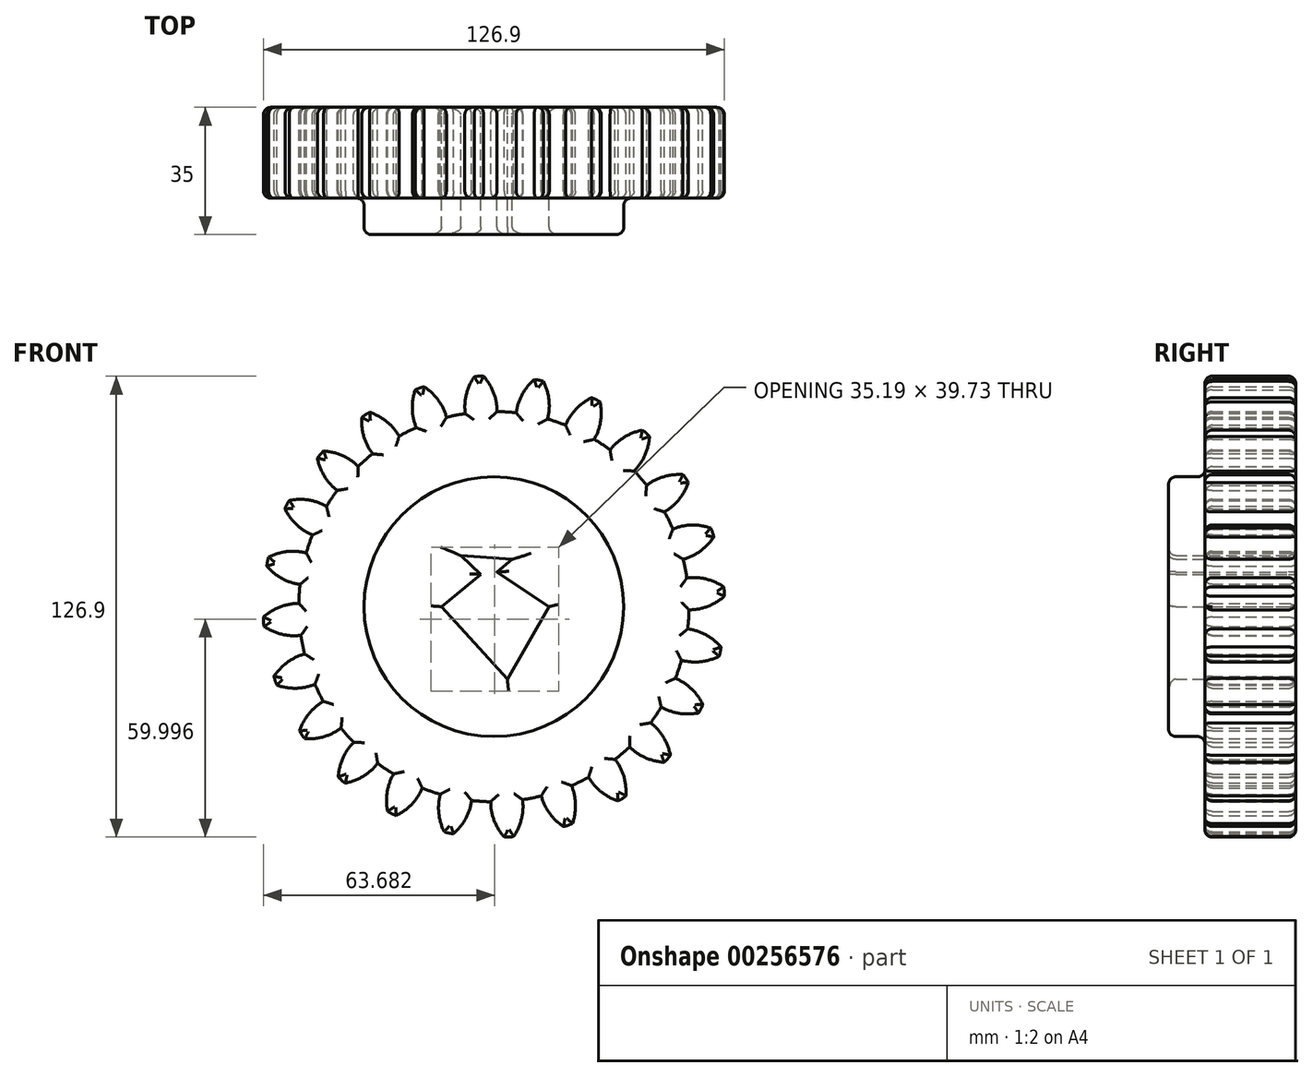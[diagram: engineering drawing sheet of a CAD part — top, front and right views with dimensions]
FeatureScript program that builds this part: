
annotation { "Feature Type Name" : "Feature", "Feature Type Description" : "" }
export const myFeature = defineFeature(function(context is Context, id is Id, definition is map)
    precondition{}
    {
        {
            var Q0;
            Q0=qCreatedBy(makeId("Front.planeOp"),FACE);
            var sketch = newSketch(context, id + "F0", { "sketchPlane" : qUnion([Q0])});
            skCircle(sketch, "E0", {"center": v(0, 0) * mm, "radius": 53.72 * mm});
            skCircle(sketch, "E1", {"center": v(0, 0) * mm, "radius": 58.67 * mm, "construction": true});
            skCircle(sketch, "E2", {"center": v(0, 0) * mm, "radius": 63.5 * mm, "construction": true});
            skLineSegment(sketch, "E3", {"start": v(0, 0) * mm, "end": v(0, 84.4) * mm, "construction": true});
            skLineSegment(sketch, "E4", {"start": v(0, 0) * mm, "end": v(-6.04, 92.1) * mm, "construction": true});
            skLineSegment(sketch, "E5", {"start": v(0, 58.67) * mm, "end": v(-60.72, 58.67) * mm, "construction": true});
            skLineSegment(sketch, "E6", {"start": v(0, 58.67) * mm, "end": v(-60.98, 36.48) * mm, "construction": true});
            skCircle(sketch, "E7", {"center": v(0, 0) * mm, "radius": 55.14 * mm, "construction": true});
            skCircle(sketch, "E8", {"center": v(0, 58.67) * mm, "radius": 14.6 * mm, "construction": true});
            skCircle(sketch, "E9", {"center": v(-13.72, 53.68) * mm, "radius": 14.6 * mm, "construction": true});
            skArc(sketch, "E10", {"start": v(0, 58.67) * mm, "mid": v(-1.2, 61.19) * mm, "end": v(-2.86, 63.44) * mm});
            skArc(sketch, "E11", {"start": v(0.88, 53.71) * mm, "mid": v(0.66, 56.23) * mm, "end": v(0, 58.67) * mm});
            skArc(sketch, "E12.MirrorCS", {"start": v(-7.66, 58.17) * mm, "mid": v(-6.8, 60.82) * mm, "end": v(-5.45, 63.27) * mm});
            skArc(sketch, "E13.MirrorCS", {"start": v(-7.88, 53.14) * mm, "mid": v(-8, 55.67) * mm, "end": v(-7.66, 58.17) * mm});
            skArc(sketch, "E14", {"start": v(-2.86, 63.44) * mm, "mid": v(-4.16, 63.43) * mm, "end": v(-5.45, 63.27) * mm});
            skCircle(sketch, "E15", {"center": v(0, 0) * mm, "radius": 35.75 * mm});
            skLineSegment(sketch, "E16", {"start": v(-3.55, 8.9) * mm, "end": v(-14.46, 0) * mm});
            skLineSegment(sketch, "E17", {"start": v(-14.46, 0) * mm, "end": v(3.69, -19.95) * mm});
            skLineSegment(sketch, "E18", {"start": v(3.69, -19.95) * mm, "end": v(15.16, 0) * mm});
            skLineSegment(sketch, "E19", {"start": v(15.16, 0) * mm, "end": v(0.8, 9.56) * mm});
            skLineSegment(sketch, "E20", {"start": v(0.8, 9.56) * mm, "end": v(5.02, 13.01) * mm});
            skLineSegment(sketch, "E21", {"start": v(-3.55, 8.9) * mm, "end": v(-9.12, 14.01) * mm});
            skLineSegment(sketch, "E22", {"start": v(-9.12, 14.01) * mm, "end": v(5.02, 13.01) * mm});
            skSolve(sketch);
        }
        {
            var Q0;
            {var subQ0=sQuery(id+"F0.wireOp",EDGE,"E0");var subQ1=makeQuery(id+"F0.imprint","INTERSECT",VERTEX,{"derivedFrom":[subQ0,sQuery(id+"F0.wireOp",EDGE,"E11")]});Q0=makeQuery(id+"F0.imprint","IMPRINT",FACE,{"disambiguationData":[TD([[makeQuery(id+"F0.imprint","IMPRINT",EDGE,{"disambiguationData":[TD([[subQ1,-1.0]])],"derivedFrom":subQ0}),1.0]])]});}
            var Q1;
            Q1=makeQuery(id+"F0.imprint","IMPRINT",FACE,{"disambiguationData":[TD([[makeQuery(id+"F0.imprint","IMPRINT",EDGE,{"derivedFrom":sQuery(id+"F0.wireOp",EDGE,"E10")}),1.0]])]});
            extrude(context, id + "F1", {"entities" : qUnion([Q0, Q1]), "depth" : 25 * mm, "offsetDistance" : 25 * mm});
        }
        {
            var Q0;
            Q0=makeQuery(id+"F1.opExtrude","SWEPT_BODY",BODY,{"disambiguationData":[OSD([sQuery(id+"F0.wireOp",EDGE,"E0"),sQuery(id+"F0.wireOp",EDGE,"E10"),sQuery(id+"F0.wireOp",EDGE,"E11"),sQuery(id+"F0.wireOp",EDGE,"E12.MirrorCS"),sQuery(id+"F0.wireOp",EDGE,"E13.MirrorCS"),sQuery(id+"F0.wireOp",EDGE,"E14")])]});
            var Q1;
            Q1=makeQuery(id+"F1.opExtrude","SWEPT_FACE",FACE,{"disambiguationData":[OSD([sQuery(id+"F0.wireOp",EDGE,"E0")])]});
            circularPattern(context, id + "F2", {"entities" : qUnion([Q0]), "axis" : qUnion([Q1]), "angle" : 360 * degree, "instanceCount" : 24, "equalSpace" : true});
        }
        {
            var Q0;
            Q0=makeQuery(id+"F0.imprint","IMPRINT",FACE,{"disambiguationData":[TD([[makeQuery(id+"F0.imprint","IMPRINT",EDGE,{"derivedFrom":sQuery(id+"F0.wireOp",EDGE,"E15")}),1.0]])]});
            extrude(context, id + "F3", {"entities" : qUnion([Q0]), "operationType" : NewBodyOperationType.ADD, "depth" : 35 * mm, "offsetDistance" : 25 * mm});
        }
        {
            var Q0;
            {var subQ0=makeQuery(id+"F1.opExtrude","CAP_FACE",FACE,{"disambiguationData":[OSD([sQuery(id+"F0.wireOp",EDGE,"E0"),sQuery(id+"F0.wireOp",EDGE,"E10"),sQuery(id+"F0.wireOp",EDGE,"E11"),sQuery(id+"F0.wireOp",EDGE,"E12.MirrorCS"),sQuery(id+"F0.wireOp",EDGE,"E13.MirrorCS"),sQuery(id+"F0.wireOp",EDGE,"E14"),sQuery(id+"F0.wireOp",EDGE,"E15")])],"isStart":false});Q0=makeQuery(id+"F3.boolean.opBoolean","MERGE",FACE,{"derivedFrom":[subQ0,makeQuery(id+"F2.opPattern","COPY",FACE,{"derivedFrom":subQ0,"instanceName":"1"}),makeQuery(id+"F2.opPattern","COPY",FACE,{"derivedFrom":subQ0,"instanceName":"2"}),makeQuery(id+"F2.opPattern","COPY",FACE,{"derivedFrom":subQ0,"instanceName":"3"}),makeQuery(id+"F2.opPattern","COPY",FACE,{"derivedFrom":subQ0,"instanceName":"4"}),makeQuery(id+"F2.opPattern","COPY",FACE,{"derivedFrom":subQ0,"instanceName":"5"}),makeQuery(id+"F2.opPattern","COPY",FACE,{"derivedFrom":subQ0,"instanceName":"6"}),makeQuery(id+"F2.opPattern","COPY",FACE,{"derivedFrom":subQ0,"instanceName":"7"}),makeQuery(id+"F2.opPattern","COPY",FACE,{"derivedFrom":subQ0,"instanceName":"8"}),makeQuery(id+"F2.opPattern","COPY",FACE,{"derivedFrom":subQ0,"instanceName":"9"}),makeQuery(id+"F2.opPattern","COPY",FACE,{"derivedFrom":subQ0,"instanceName":"10"}),makeQuery(id+"F2.opPattern","COPY",FACE,{"derivedFrom":subQ0,"instanceName":"11"}),makeQuery(id+"F2.opPattern","COPY",FACE,{"derivedFrom":subQ0,"instanceName":"12"}),makeQuery(id+"F2.opPattern","COPY",FACE,{"derivedFrom":subQ0,"instanceName":"13"}),makeQuery(id+"F2.opPattern","COPY",FACE,{"derivedFrom":subQ0,"instanceName":"14"}),makeQuery(id+"F2.opPattern","COPY",FACE,{"derivedFrom":subQ0,"instanceName":"15"}),makeQuery(id+"F2.opPattern","COPY",FACE,{"derivedFrom":subQ0,"instanceName":"16"}),makeQuery(id+"F2.opPattern","COPY",FACE,{"derivedFrom":subQ0,"instanceName":"17"}),makeQuery(id+"F2.opPattern","COPY",FACE,{"derivedFrom":subQ0,"instanceName":"18"}),makeQuery(id+"F2.opPattern","COPY",FACE,{"derivedFrom":subQ0,"instanceName":"19"}),makeQuery(id+"F2.opPattern","COPY",FACE,{"derivedFrom":subQ0,"instanceName":"20"}),makeQuery(id+"F2.opPattern","COPY",FACE,{"derivedFrom":subQ0,"instanceName":"21"}),makeQuery(id+"F2.opPattern","COPY",FACE,{"derivedFrom":subQ0,"instanceName":"22"}),makeQuery(id+"F2.opPattern","COPY",FACE,{"derivedFrom":subQ0,"instanceName":"23"})]});}
            var Q1;
            {var subQ0=sQuery(id+"F0.wireOp",EDGE,"E15");var subQ1=makeQuery(id+"F1.opExtrude","CAP_FACE",FACE,{"disambiguationData":[OSD([sQuery(id+"F0.wireOp",EDGE,"E0"),sQuery(id+"F0.wireOp",EDGE,"E10"),sQuery(id+"F0.wireOp",EDGE,"E11"),sQuery(id+"F0.wireOp",EDGE,"E12.MirrorCS"),sQuery(id+"F0.wireOp",EDGE,"E13.MirrorCS"),sQuery(id+"F0.wireOp",EDGE,"E14"),subQ0])],"isStart":true});Q1=makeQuery(id+"F3.boolean.opBoolean","MERGE",FACE,{"derivedFrom":[subQ1,makeQuery(id+"F2.opPattern","COPY",FACE,{"derivedFrom":subQ1,"instanceName":"1"}),makeQuery(id+"F2.opPattern","COPY",FACE,{"derivedFrom":subQ1,"instanceName":"2"}),makeQuery(id+"F2.opPattern","COPY",FACE,{"derivedFrom":subQ1,"instanceName":"3"}),makeQuery(id+"F2.opPattern","COPY",FACE,{"derivedFrom":subQ1,"instanceName":"4"}),makeQuery(id+"F2.opPattern","COPY",FACE,{"derivedFrom":subQ1,"instanceName":"5"}),makeQuery(id+"F2.opPattern","COPY",FACE,{"derivedFrom":subQ1,"instanceName":"6"}),makeQuery(id+"F2.opPattern","COPY",FACE,{"derivedFrom":subQ1,"instanceName":"7"}),makeQuery(id+"F2.opPattern","COPY",FACE,{"derivedFrom":subQ1,"instanceName":"8"}),makeQuery(id+"F2.opPattern","COPY",FACE,{"derivedFrom":subQ1,"instanceName":"9"}),makeQuery(id+"F2.opPattern","COPY",FACE,{"derivedFrom":subQ1,"instanceName":"10"}),makeQuery(id+"F2.opPattern","COPY",FACE,{"derivedFrom":subQ1,"instanceName":"11"}),makeQuery(id+"F2.opPattern","COPY",FACE,{"derivedFrom":subQ1,"instanceName":"12"}),makeQuery(id+"F2.opPattern","COPY",FACE,{"derivedFrom":subQ1,"instanceName":"13"}),makeQuery(id+"F2.opPattern","COPY",FACE,{"derivedFrom":subQ1,"instanceName":"14"}),makeQuery(id+"F2.opPattern","COPY",FACE,{"derivedFrom":subQ1,"instanceName":"15"}),makeQuery(id+"F2.opPattern","COPY",FACE,{"derivedFrom":subQ1,"instanceName":"16"}),makeQuery(id+"F2.opPattern","COPY",FACE,{"derivedFrom":subQ1,"instanceName":"17"}),makeQuery(id+"F2.opPattern","COPY",FACE,{"derivedFrom":subQ1,"instanceName":"18"}),makeQuery(id+"F2.opPattern","COPY",FACE,{"derivedFrom":subQ1,"instanceName":"19"}),makeQuery(id+"F2.opPattern","COPY",FACE,{"derivedFrom":subQ1,"instanceName":"20"}),makeQuery(id+"F2.opPattern","COPY",FACE,{"derivedFrom":subQ1,"instanceName":"21"}),makeQuery(id+"F2.opPattern","COPY",FACE,{"derivedFrom":subQ1,"instanceName":"22"}),makeQuery(id+"F2.opPattern","COPY",FACE,{"derivedFrom":subQ1,"instanceName":"23"}),makeQuery(id+"F3.opExtrude","CAP_FACE",FACE,{"disambiguationData":[OSD([subQ0,sQuery(id+"F0.wireOp",EDGE,"E16"),sQuery(id+"F0.wireOp",EDGE,"E17"),sQuery(id+"F0.wireOp",EDGE,"E18"),sQuery(id+"F0.wireOp",EDGE,"E19"),sQuery(id+"F0.wireOp",EDGE,"E20"),sQuery(id+"F0.wireOp",EDGE,"E21"),sQuery(id+"F0.wireOp",EDGE,"E22")])],"isStart":true})]});}
            var Q2;
            Q2=makeQuery(id+"F3.opExtrude","CAP_FACE",FACE,{"disambiguationData":[OSD([sQuery(id+"F0.wireOp",EDGE,"E15"),sQuery(id+"F0.wireOp",EDGE,"E16"),sQuery(id+"F0.wireOp",EDGE,"E17"),sQuery(id+"F0.wireOp",EDGE,"E18"),sQuery(id+"F0.wireOp",EDGE,"E19"),sQuery(id+"F0.wireOp",EDGE,"E20"),sQuery(id+"F0.wireOp",EDGE,"E21"),sQuery(id+"F0.wireOp",EDGE,"E22")])],"isStart":false});
            fillet(context, id + "F4", {"entities" : qUnion([Q0, Q1, Q2]), "radius" : 2 * mm, "tangentPropagation" : true, "allowEdgeOverflow" : false});
        }
    });
